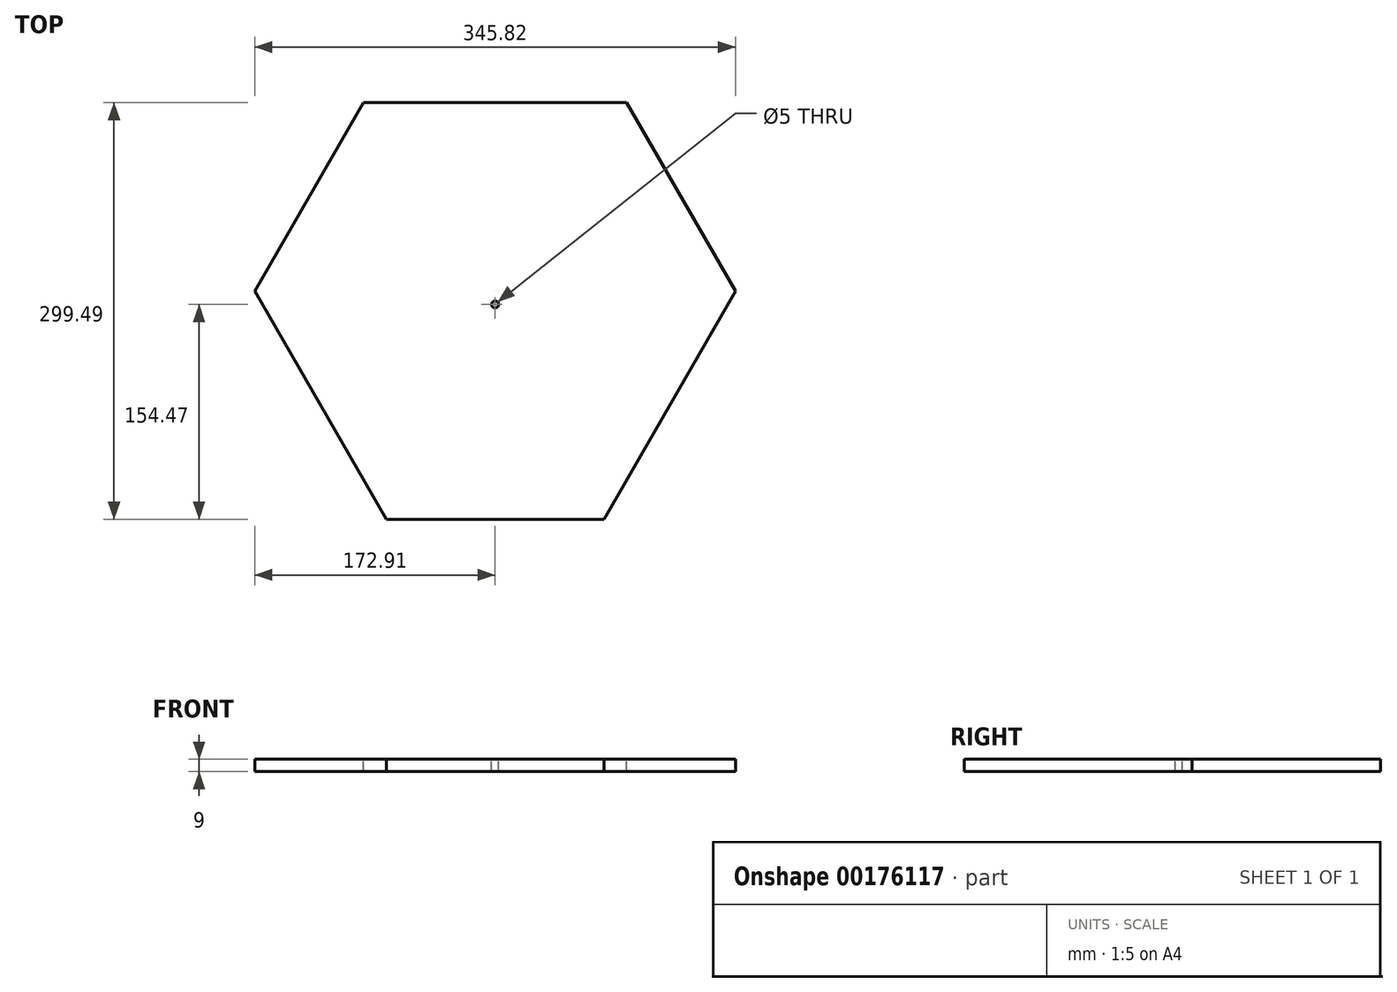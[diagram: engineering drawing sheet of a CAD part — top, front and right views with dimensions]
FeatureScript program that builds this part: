
annotation { "Feature Type Name" : "Feature", "Feature Type Description" : "" }
export const myFeature = defineFeature(function(context is Context, id is Id, definition is map)
    precondition{}
    {
        {
            var Q0;
            Q0=qCreatedBy(makeId("Top.planeOp"),FACE);
            var sketch = newSketch(context, id + "F0", { "sketchPlane" : qUnion([Q0])});
            skCircle(sketch, "E0.cCircle", {"center": v(0, 0) * mm, "radius": 145.02 * mm, "construction": true});
            skLineSegment(sketch, "E0.0", {"start": v(-60, 145.02) * mm, "end": v(60, 145.02) * mm});
            skLineSegment(sketch, "E0.1", {"start": v(155.59, -20.55) * mm, "end": v(95.59, -124.47) * mm});
            skLineSegment(sketch, "E0.2", {"start": v(-95.59, -124.47) * mm, "end": v(-155.59, -20.55) * mm});
            skPoint(sketch, "E0.0.midPoint", {"position": v(0, 145.02) * mm});
            skCircle(sketch, "E1.cCircle", {"center": v(0, 0) * mm, "radius": 124.47 * mm, "construction": true});
            skLineSegment(sketch, "E1.0", {"start": v(95.59, -124.47) * mm, "end": v(-95.59, -124.47) * mm});
            skLineSegment(sketch, "E1.1", {"start": v(-155.59, -20.55) * mm, "end": v(-60, 145.02) * mm});
            skLineSegment(sketch, "E1.2", {"start": v(60, 145.02) * mm, "end": v(155.59, -20.55) * mm});
            skPoint(sketch, "E1.0.midPoint", {"position": v(0, -124.47) * mm});
            skPoint(sketch, "E2.orphan", {"position": v(-251.18, 145.02) * mm});
            skPoint(sketch, "E3.orphan", {"position": v(-215.59, -124.47) * mm});
            skPoint(sketch, "E4.orphan", {"position": v(0, -290.03) * mm});
            skPoint(sketch, "E5.orphan", {"position": v(215.59, -124.47) * mm});
            skPoint(sketch, "E6.orphan", {"position": v(251.18, 145.02) * mm});
            skPoint(sketch, "E7.orphan", {"position": v(0, 248.94) * mm});
            skSolve(sketch);
        }
        {
            var Q0;
            Q0=makeQuery(id+"F0.imprint","IMPRINT",FACE,{"disambiguationData":[TD([[makeQuery(id+"F0.imprint","IMPRINT",EDGE,{"derivedFrom":sQuery(id+"F0.wireOp",EDGE,"E0.0")}),-1.0]])]});
            extrude(context, id + "F1", {"entities" : qUnion([Q0]), "depth" : 9 * mm});
        }
        {
            var Q0;
            Q0=makeQuery(id+"F1.opExtrude","CAP_FACE",FACE,{"disambiguationData":[OSD([sQuery(id+"F0.wireOp",EDGE,"E0.0"),sQuery(id+"F0.wireOp",EDGE,"E0.1"),sQuery(id+"F0.wireOp",EDGE,"E0.2"),sQuery(id+"F0.wireOp",EDGE,"E1.0"),sQuery(id+"F0.wireOp",EDGE,"E1.1"),sQuery(id+"F0.wireOp",EDGE,"E1.2")])],"isStart":false});
            var sketch = newSketch(context, id + "F2", { "sketchPlane" : qUnion([Q0])});
            skLineSegment(sketch, "E8.0", {"start": v(-172.9, 9.45) * mm, "end": v(-94.64, 145.02) * mm});
            skLineSegment(sketch, "E9.0", {"start": v(94.64, 145.02) * mm, "end": v(172.9, 9.45) * mm});
            skLineSegment(sketch, "E10.0", {"start": v(78.27, -154.47) * mm, "end": v(-78.27, -154.47) * mm});
            skLineSegment(sketch, "E11", {"start": v(-155.59, -20.55) * mm, "end": v(-172.9, 9.45) * mm});
            skLineSegment(sketch, "E12", {"start": v(-60, 145.02) * mm, "end": v(-94.64, 145.02) * mm});
            skLineSegment(sketch, "E13", {"start": v(60, 145.02) * mm, "end": v(94.64, 145.02) * mm});
            skLineSegment(sketch, "E14", {"start": v(155.59, -20.55) * mm, "end": v(172.9, 9.45) * mm});
            skLineSegment(sketch, "E15", {"start": v(-95.59, -124.47) * mm, "end": v(-78.27, -154.47) * mm});
            skLineSegment(sketch, "E16", {"start": v(95.59, -124.47) * mm, "end": v(78.27, -154.47) * mm});
            skSolve(sketch);
        }
        {
            var Q0;
            Q0=makeQuery(id+"F2.imprint","IMPRINT",FACE,{"disambiguationData":[TD([[makeQuery(id+"F2.imprint","IMPRINT",EDGE,{"derivedFrom":sQuery(id+"F2.wireOp",EDGE,"E8.0")}),-1.0]])]});
            var Q1;
            Q1=makeQuery(id+"F2.imprint","IMPRINT",FACE,{"disambiguationData":[TD([[makeQuery(id+"F2.imprint","IMPRINT",EDGE,{"derivedFrom":sQuery(id+"F2.wireOp",EDGE,"E9.0")}),-1.0]])]});
            var Q2;
            Q2=makeQuery(id+"F2.imprint","IMPRINT",FACE,{"disambiguationData":[TD([[makeQuery(id+"F2.imprint","IMPRINT",EDGE,{"derivedFrom":sQuery(id+"F2.wireOp",EDGE,"E10.0")}),-1.0]])]});
            extrude(context, id + "F3", {"entities" : qUnion([Q0, Q1, Q2]), "operationType" : NewBodyOperationType.ADD, "oppositeDirection" : true, "depth" : 9 * mm});
        }
        {
            var Q0;
            {var subQ0=sQuery(id+"F0.wireOp",EDGE,"E1.0");var subQ1=sQuery(id+"F0.wireOp",EDGE,"E1.2");var subQ2=sQuery(id+"F0.wireOp",EDGE,"E1.1");Q0=makeQuery(id+"F3.boolean.opBoolean","MERGE",FACE,{"derivedFrom":[makeQuery(id+"F1.opExtrude","CAP_FACE",FACE,{"disambiguationData":[OSD([sQuery(id+"F0.wireOp",EDGE,"E0.0"),sQuery(id+"F0.wireOp",EDGE,"E0.1"),sQuery(id+"F0.wireOp",EDGE,"E0.2"),subQ0,subQ2,subQ1])],"isStart":false}),makeQuery(id+"F3.opExtrude","CAP_FACE",FACE,{"disambiguationData":[OSD([subQ2,sQuery(id+"F2.wireOp",EDGE,"E8.0"),sQuery(id+"F2.wireOp",EDGE,"E11"),sQuery(id+"F2.wireOp",EDGE,"E12")])],"isStart":true}),makeQuery(id+"F3.opExtrude","CAP_FACE",FACE,{"disambiguationData":[OSD([subQ1,sQuery(id+"F2.wireOp",EDGE,"E9.0"),sQuery(id+"F2.wireOp",EDGE,"E13"),sQuery(id+"F2.wireOp",EDGE,"E14")])],"isStart":true}),makeQuery(id+"F3.opExtrude","CAP_FACE",FACE,{"disambiguationData":[OSD([subQ0,sQuery(id+"F2.wireOp",EDGE,"E10.0"),sQuery(id+"F2.wireOp",EDGE,"E15"),sQuery(id+"F2.wireOp",EDGE,"E16")])],"isStart":true})]});}
            var sketch = newSketch(context, id + "F4", { "sketchPlane" : qUnion([Q0])});
            skCircle(sketch, "E17", {"center": v(0, 0) * mm, "radius": 2.5 * mm});
            skSolve(sketch);
        }
        {
            var Q0;
            Q0 = qSketchRegion(id + "F4", true);
            extrude(context, id + "F5", {"entities" : qUnion([Q0]), "operationType" : NewBodyOperationType.REMOVE, "oppositeDirection" : true, "depth" : 25 * mm});
        }
    });
